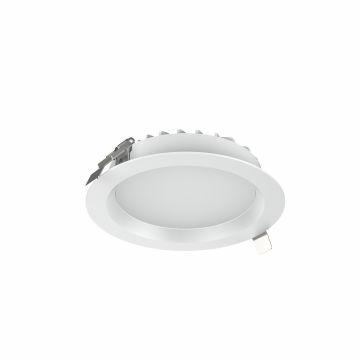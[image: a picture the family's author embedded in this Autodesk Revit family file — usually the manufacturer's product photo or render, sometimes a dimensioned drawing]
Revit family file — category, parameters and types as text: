
# Revit family: Lighting-CommercialSector-GEWISS-ELIA-DL-LED_DOWNLIGHT
name_source: partatom
category: Apparecchi per illuminazione
units: mm (PartAtom-declared; Revit-internal decimal feet)

## family parameters
Condiviso = No
Host = Superficie
Punto di calcolo locali = Sì
Quota connettore circolare = Usa diametro
Sorgente d'illuminazione = Sì
Taglio con vuoti quando caricato = No
Tipo di parte = Normale

## types (8) — shared parameters
Angolo inclinazione = -90.00°
Application = Indoor
Catalogue = LIGHTING
Catalogue Range = ELIA DL
Colour = White
Colour temperature = 4000K
Colour temperature: = 4000K
Dimensions (mm) = Standard
Emetti da lunghezza linea = 610 mm
FORO_CONTROSOFFITTO = 80 mm  [stored 0.262467 ft]
File diagramma fotometrico = GWF1511QA940.IES
Filtro dei colori = 16777215
IDF = 46d3fa0c-6ffa-4080-9a39-1d8cfdb7318d
IDT = 67a9fb0b-5b9a-414d-aab5-ce16ea450aa5
IP degree = IP40 - IP54
Immagine tipo = ELIA_DL.jpg
Installation = Flush mounted
Insulation class = II
LARGHEZZA_FORO = 820 mm
LED = <Per categoria>
LED Life time (L80B50) = L80 B50 (Tq25°) = 50.000h
LUNGHEZZA FORO = 969 mm
L_lampada = 1500 mm  [stored 4.92126 ft]
Lamp = LED
Operating temperature: = -20° +45°
Optic = Diffusing opal
POSIZIONE = 80000
Produttore = GEWISS S.p.A.
Prospetto di default = 1219 mm
SEO = Flush mounted
STRUTTURA = <Per categoria>
Shock resistance = IK06
Technical sheet = https://www.gewiss.com
Type of lamp = LED
Type of light source = LED - Not replaceable
Typology = Flush mounted
URL = https://www.gewiss.com
Variazione temperatura colore lampada con luminosità attenuata = <Nessuno>
Version file RFA = 20.0
Voltage = 220-240 VÂ
Warranty = 5 years
Weight (kg) = 0,8
Weight (kg): = 0,8
Working temperature = -20° +45°

## per-type parameters (varying)
| type | Descrizione | Lumen output (lm) | Modello | System power |
| GWF1510QA940 - ELIA DL L2 40K  OPAL ON/OFF CRI90 | ELIA DL L2 40K  OPAL ON/OFF CRI90 | 3200 | GWF1510QA940 | 35W |
| GWF1510MA840 - ELIA DL M2 40K OPAL ON/OFF CRI80 | ELIA DL M2 40K OPAL ON/OFF CRI80 | 2600 | GWF1510MA840 | 25W |
| GWF1511MA940 - ELIA DL M2 40K OPAL DALI CRI90 | ELIA DL M2 40K OPAL DALI CRI90 | 2340 | GWF1511MA940 | 25W |
| GWF1510QA840 - ELIA DL L2 40K  OPAL ON/OFF CRI80 | ELIA DL L2 40K  OPAL ON/OFF CRI80 | 3550 | GWF1510QA840 | 35W |
| GWF1510MA940 - ELIA DL M2 40K  OPAL ON/OFF CRI90 | ELIA DL M2 40K  OPAL ON/OFF CRI90 | 2340 | GWF1510MA940 | 25W |
| GWF1511QA840 - ELIA DL L2 40K OPAL DALI CRI80 | ELIA DL L2 40K OPAL DALI CRI80 | 3550 | GWF1511QA840 | 35W |
| GWF1511MA840 - ELIA DL M2 40K OPAL DALI CRI80 | ELIA DL M2 40K OPAL DALI CRI80 | 2600 | GWF1511MA840 | 25W |
| GWF1511QA940 - ELIA DL L2 40K OPAL DALI CRI90 | ELIA DL L2 40K OPAL DALI CRI90 | 3200 | GWF1511QA940 | 35W |

note: [stored X ft] marks values corroborated as IEEE doubles in the binary element streams (Revit-internal decimal feet)
